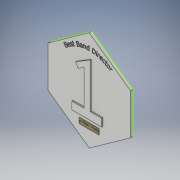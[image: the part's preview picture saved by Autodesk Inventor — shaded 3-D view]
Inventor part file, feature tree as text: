
AUTODESK INVENTOR PART (.ipt)
format: ipt  version: 2018 (Build 220112000, 112)  size: 1,182,720 bytes
history: native  units: in
note: dims shown in document units (in); Inventor stores cm internally (conversion verified against a paired STEP export)
features: sketch x12, extrude x5, hole x1, plane x1
ambient origin geometry x8: Origin, YZ Plane, XZ Plane, XY Plane, X Axis, Y Axis, Z Axis, Center Point
bodies: Solid1 (feature_tree)
feature tree (19):
  sketch  "Sketch1"  dims[d1=12.0in d2=0.0in d3=1.0in d4=0.0in]
  extrude  "Extrusion1"  Depth=12.0in TaperAngle=0.0deg
  extrude  "Extrusion2"  Depth=5.0in
  sketch  "Sketch6"  dims[d21=6.0in d22=1.0in d23=0.0in]
  sketch  "Sketch7"  dims[d24=1.0in d25=0.0in d89=5.0in d90=0.0in]
  sketch  "Sketch8"  dims[d5=1.0in d6=1.0in]
  sketch  "Sketch9"
  hole  "Hole2"  [1 undecoded]
  extrude  "Extrusion3"  Depth=5.0in TaperAngle=0.0deg
  sketch  "Sketch11"
  extrude  "Extrusion4"  Depth=1.0in
  sketch  "Sketch12"
  sketch  "Sketch14"
  sketch  "Sketch15"
  plane  "Work Plane1"
  extrude  "Extrusion7"  [1 undecoded]
  sketch  "Sketch5"  dims[d13=0.196in d14=0.5in d15=5.0in d16=0.25in d17=0.5635in d18=1.0in d19=0.8108in d20=6.0in]
  sketch  "Sketch10"
  sketch  "Sketch16"
note: 2 required parameter values undecoded (feature->parameter linkage not recoverable at this tier; creation-order binding heuristic only, values carry confidence <= 0.55)
